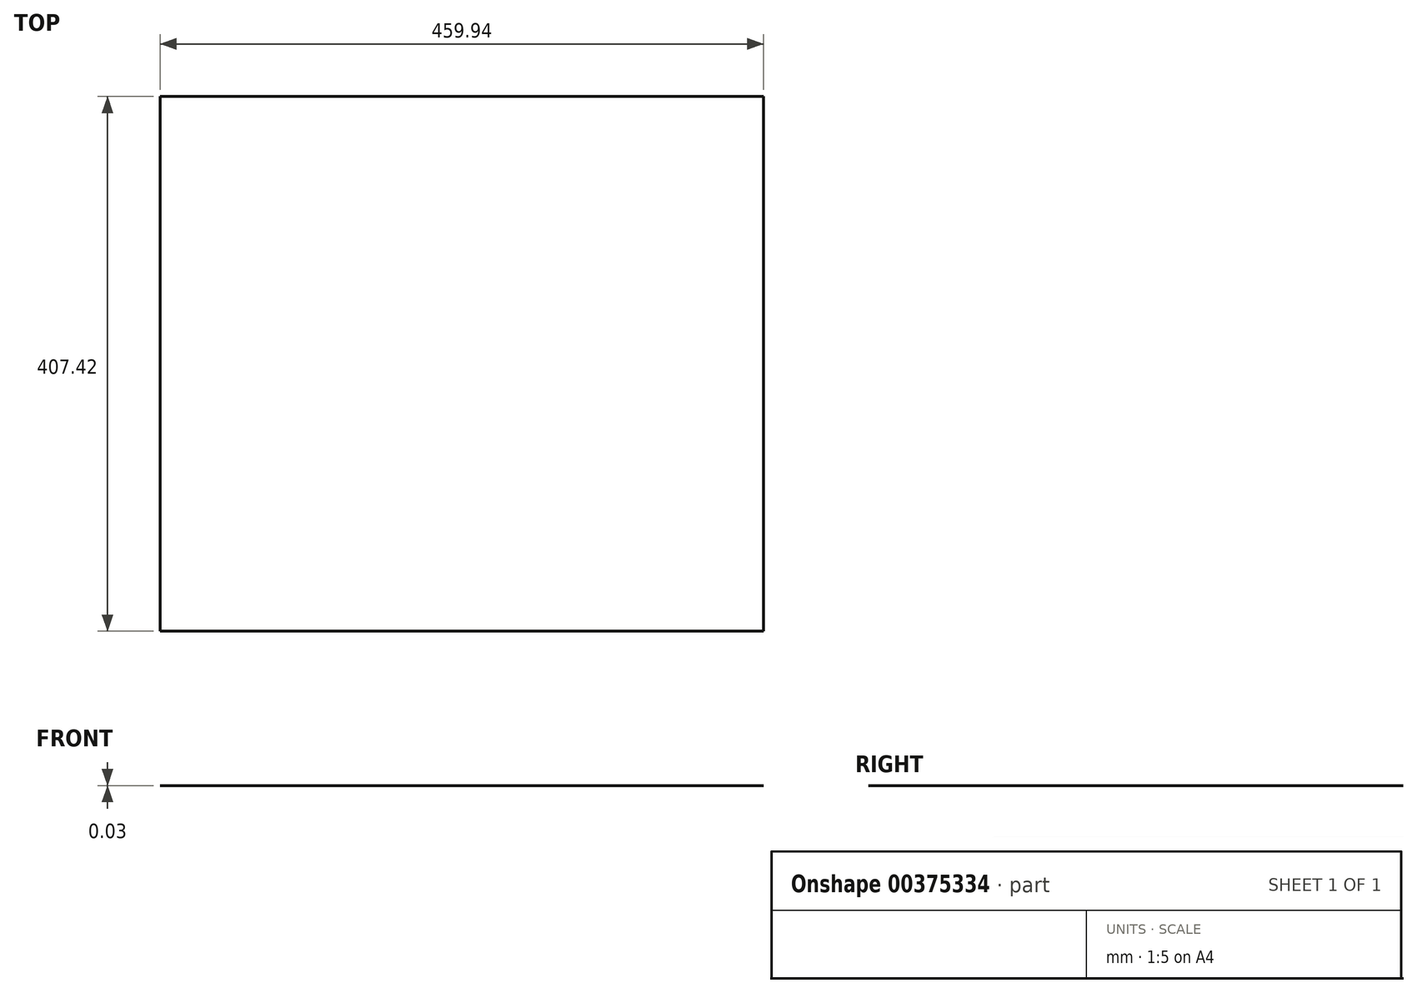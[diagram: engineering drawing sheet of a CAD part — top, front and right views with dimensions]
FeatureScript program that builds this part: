
annotation { "Feature Type Name" : "Feature", "Feature Type Description" : "" }
export const myFeature = defineFeature(function(context is Context, id is Id, definition is map)
    precondition{}
    {
        {
            var Q0;
            Q0=qCreatedBy(makeId("Top.planeOp"),FACE);
            var sketch = newSketch(context, id + "F0", { "sketchPlane" : qUnion([Q0])});
            skLineSegment(sketch, "E0.bottom", {"start": v(-433.65, -69.04) * mm, "end": v(26.29, -69.04) * mm});
            skLineSegment(sketch, "E0.top", {"start": v(-433.65, 338.38) * mm, "end": v(26.29, 338.38) * mm});
            skLineSegment(sketch, "E0.left", {"start": v(-433.65, -69.04) * mm, "end": v(-433.65, 338.38) * mm});
            skLineSegment(sketch, "E0.right", {"start": v(26.29, -69.04) * mm, "end": v(26.29, 338.38) * mm});
            skSolve(sketch);
        }
        {
            var Q0;
            Q0=makeQuery(id+"F0.imprint","IMPRINT",FACE,{"disambiguationData":[TD([[makeQuery(id+"F0.imprint","IMPRINT",EDGE,{"derivedFrom":sQuery(id+"F0.wireOp",EDGE,"E0.bottom")}),1.0]])]});
            extrude(context, id + "F1", {"entities" : qUnion([Q0]), "depth" : 0.03 * mm});
        }
        {
            var Q0;
            Q0=qCreatedBy(makeId("Top.planeOp"),FACE);
            var sketch = newSketch(context, id + "F2", { "sketchPlane" : qUnion([Q0])});
            skLineSegment(sketch, "E1", {"start": v(87.45, 112.84) * mm, "end": v(87.45, -85.72) * mm});
            skSolve(sketch);
        }
        {
            var Q0;
            Q0=sQuery(id+"F2.wireOp",EDGE,"E1");
            extrude(context, id + "F3", {"bodyType" : ToolBodyType.SURFACE, "surfaceEntities" : qUnion([Q0]), "depth" : 0.25 * mm});
        }
        {
            var Q0;
            Q0=qCreatedBy(makeId("Top.planeOp"),FACE);
            var sketch = newSketch(context, id + "F4", { "sketchPlane" : qUnion([Q0])});
            skLineSegment(sketch, "E2", {"start": v(127.3, 108.38) * mm, "end": v(127.3, 0) * mm});
            skSolve(sketch);
        }
        {
            var Q0;
            Q0=sQuery(id+"F4.wireOp",EDGE,"E2");
            extrude(context, id + "F5", {"bodyType" : ToolBodyType.SURFACE, "surfaceEntities" : qUnion([Q0]), "depth" : 0.25 * mm});
        }
    });
